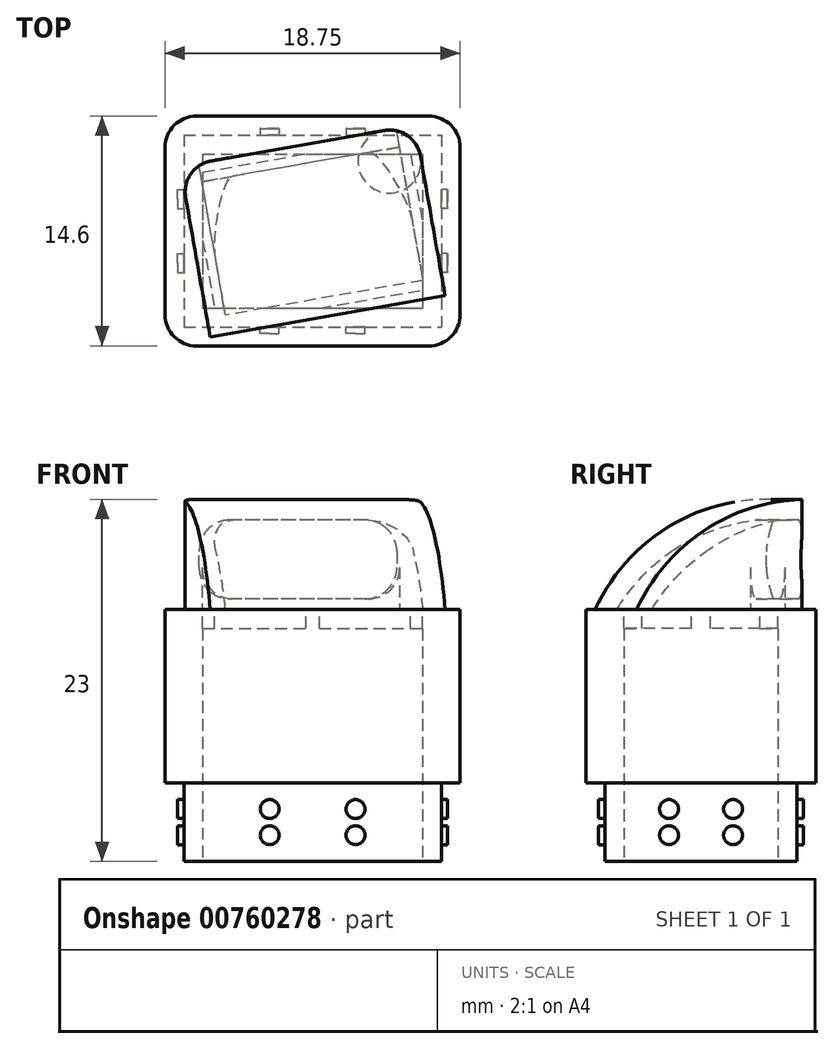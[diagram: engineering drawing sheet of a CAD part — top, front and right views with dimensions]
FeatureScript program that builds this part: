
annotation { "Feature Type Name" : "Feature", "Feature Type Description" : "" }
export const myFeature = defineFeature(function(context is Context, id is Id, definition is map)
    precondition{}
    {
        {
            var Q0;
            Q0=qCreatedBy(makeId("Top.planeOp"),FACE);
            var sketch = newSketch(context, id + "F0", { "sketchPlane" : qUnion([Q0])});
            skLineSegment(sketch, "E0.bottom", {"start": v(-6.9, 7.84) * mm, "end": v(9.85, 7.84) * mm, "construction": true});
            skLineSegment(sketch, "E0.top", {"start": v(-6.9, -4.76) * mm, "end": v(9.85, -4.76) * mm, "construction": true});
            skLineSegment(sketch, "E0.left", {"start": v(-6.9, 7.84) * mm, "end": v(-6.9, -4.76) * mm, "construction": true});
            skLineSegment(sketch, "E0.right", {"start": v(9.85, 7.84) * mm, "end": v(9.85, -4.76) * mm, "construction": true});
            skLineSegment(sketch, "E1.0", {"start": v(-6.7, 7.64) * mm, "end": v(9.65, 7.64) * mm});
            skLineSegment(sketch, "E1.1", {"start": v(-6.7, 7.64) * mm, "end": v(-6.7, -4.56) * mm});
            skLineSegment(sketch, "E1.2", {"start": v(-6.7, -4.56) * mm, "end": v(9.65, -4.56) * mm});
            skLineSegment(sketch, "E1.3", {"start": v(9.65, 7.64) * mm, "end": v(9.65, -4.56) * mm});
            skLineSegment(sketch, "E2.0", {"start": v(-5.5, 6.44) * mm, "end": v(8.45, 6.44) * mm});
            skLineSegment(sketch, "E2.1", {"start": v(-5.5, 6.44) * mm, "end": v(-5.5, -3.36) * mm});
            skLineSegment(sketch, "E2.2", {"start": v(-5.5, -3.36) * mm, "end": v(8.45, -3.36) * mm});
            skLineSegment(sketch, "E2.3", {"start": v(8.45, 6.44) * mm, "end": v(8.45, -3.36) * mm});
            skSolve(sketch);
        }
        {
            var Q0;
            Q0 = qSketchRegion(id + "F0", true);
            extrude(context, id + "F1", {"entities" : qUnion([Q0]), "depth" : 5 * mm, "offsetDistance" : 25 * mm});
        }
        {
            var Q0;
            Q0=makeQuery(id+"F1.opExtrude","CAP_FACE",FACE,{"disambiguationData":[OSD([sQuery(id+"F0.wireOp",EDGE,"E1.0"),sQuery(id+"F0.wireOp",EDGE,"E1.1"),sQuery(id+"F0.wireOp",EDGE,"E1.2"),sQuery(id+"F0.wireOp",EDGE,"E1.3"),sQuery(id+"F0.wireOp",EDGE,"E2.0"),sQuery(id+"F0.wireOp",EDGE,"E2.1"),sQuery(id+"F0.wireOp",EDGE,"E2.2"),sQuery(id+"F0.wireOp",EDGE,"E2.3")])],"isStart":false});
            var sketch = newSketch(context, id + "F2", { "sketchPlane" : qUnion([Q0])});
            skLineSegment(sketch, "E3.0", {"start": v(-5.5, 6.44) * mm, "end": v(-5.5, -3.36) * mm});
            skLineSegment(sketch, "E3.1", {"start": v(-5.5, 6.44) * mm, "end": v(8.45, 6.44) * mm});
            skLineSegment(sketch, "E3.2", {"start": v(8.45, 6.44) * mm, "end": v(8.45, -3.36) * mm});
            skLineSegment(sketch, "E3.3", {"start": v(-5.5, -3.36) * mm, "end": v(8.45, -3.36) * mm});
            skLineSegment(sketch, "E4.0", {"start": v(-6.7, 7.64) * mm, "end": v(9.65, 7.64) * mm, "construction": true});
            skLineSegment(sketch, "E4.1", {"start": v(-6.7, 7.64) * mm, "end": v(-6.7, -4.56) * mm, "construction": true});
            skLineSegment(sketch, "E4.2", {"start": v(-6.7, -4.56) * mm, "end": v(9.65, -4.56) * mm, "construction": true});
            skLineSegment(sketch, "E4.3", {"start": v(9.65, 7.64) * mm, "end": v(9.65, -4.56) * mm, "construction": true});
            skLineSegment(sketch, "E5.0", {"start": v(-7.9, 8.84) * mm, "end": v(10.85, 8.84) * mm});
            skLineSegment(sketch, "E5.1", {"start": v(-7.9, 8.84) * mm, "end": v(-7.9, -5.76) * mm});
            skLineSegment(sketch, "E5.2", {"start": v(-7.9, -5.76) * mm, "end": v(10.85, -5.76) * mm});
            skLineSegment(sketch, "E5.3", {"start": v(10.85, 8.84) * mm, "end": v(10.85, -5.76) * mm});
            skSolve(sketch);
        }
        {
            var Q0;
            Q0 = qSketchRegion(id + "F2", true);
            extrude(context, id + "F3", {"entities" : qUnion([Q0]), "operationType" : NewBodyOperationType.ADD, "depth" : 9.8 * mm, "offsetDistance" : 25 * mm});
        }
        {
            var Q0;
            Q0=makeQuery(id+"F3.opExtrude","CAP_FACE",FACE,{"disambiguationData":[OSD([sQuery(id+"F2.wireOp",EDGE,"E3.0"),sQuery(id+"F2.wireOp",EDGE,"E3.1"),sQuery(id+"F2.wireOp",EDGE,"E3.2"),sQuery(id+"F2.wireOp",EDGE,"E3.3"),sQuery(id+"F2.wireOp",EDGE,"E5.0"),sQuery(id+"F2.wireOp",EDGE,"E5.1"),sQuery(id+"F2.wireOp",EDGE,"E5.2"),sQuery(id+"F2.wireOp",EDGE,"E5.3")])],"isStart":false});
            var sketch = newSketch(context, id + "F4", { "sketchPlane" : qUnion([Q0])});
            skLineSegment(sketch, "E6.0", {"start": v(-7.9, 8.84) * mm, "end": v(-7.9, -5.76) * mm});
            skLineSegment(sketch, "E6.1", {"start": v(-7.9, 8.84) * mm, "end": v(10.85, 8.84) * mm});
            skLineSegment(sketch, "E6.2", {"start": v(10.85, 8.84) * mm, "end": v(10.85, -5.76) * mm});
            skLineSegment(sketch, "E6.3", {"start": v(-7.9, -5.76) * mm, "end": v(10.85, -5.76) * mm});
            skSolve(sketch);
        }
        {
            var Q0;
            Q0 = qSketchRegion(id + "F4", true);
            extrude(context, id + "F5", {"entities" : qUnion([Q0]), "operationType" : NewBodyOperationType.ADD, "depth" : 1.2 * mm, "offsetDistance" : 25 * mm});
        }
        {
            var Q0;
            Q0=makeQuery(id+"F5.opExtrude","CAP_FACE",FACE,{"disambiguationData":[OSD([sQuery(id+"F4.wireOp",EDGE,"E6.0"),sQuery(id+"F4.wireOp",EDGE,"E6.1"),sQuery(id+"F4.wireOp",EDGE,"E6.2"),sQuery(id+"F4.wireOp",EDGE,"E6.3")])],"isStart":false});
            var sketch = newSketch(context, id + "F6", { "sketchPlane" : qUnion([Q0])});
            skLineSegment(sketch, "E7.0", {"start": v(-7.9, 8.84) * mm, "end": v(-7.9, -5.76) * mm, "construction": true});
            skLineSegment(sketch, "E7.1", {"start": v(-7.9, -5.76) * mm, "end": v(10.85, -5.76) * mm, "construction": true});
            skLineSegment(sketch, "E8.0", {"start": v(-5.5, 6.44) * mm, "end": v(8.45, 6.44) * mm, "construction": true});
            skLineSegment(sketch, "E8.1", {"start": v(-5.5, 6.44) * mm, "end": v(-5.5, -3.36) * mm, "construction": true});
            skLineSegment(sketch, "E8.2", {"start": v(8.45, 6.44) * mm, "end": v(8.45, -3.36) * mm, "construction": true});
            skLineSegment(sketch, "E8.3", {"start": v(-5.5, -3.36) * mm, "end": v(8.45, -3.36) * mm, "construction": true});
            skLineSegment(sketch, "E9", {"start": v(-7.9, 8.84) * mm, "end": v(10.85, -5.76) * mm, "construction": true});
            skLineSegment(sketch, "E10.bottom", {"start": v(9.2, -2.08) * mm, "end": v(-4.54, -4.5) * mm, "construction": true});
            skLineSegment(sketch, "E10.top", {"start": v(7.5, 7.57) * mm, "end": v(-6.24, 5.15) * mm, "construction": true});
            skLineSegment(sketch, "E10.left", {"start": v(9.2, -2.08) * mm, "end": v(7.5, 7.57) * mm, "construction": true});
            skLineSegment(sketch, "E10.right", {"start": v(-4.54, -4.5) * mm, "end": v(-6.24, 5.15) * mm, "construction": true});
            skPoint(sketch, "E10.middle", {"position": v(1.48, 1.54) * mm});
            skLineSegment(sketch, "E11.0", {"start": v(-5.03, -5.2) * mm, "end": v(-6.94, 5.64) * mm});
            skLineSegment(sketch, "E11.1", {"start": v(9.9, -2.57) * mm, "end": v(-5.03, -5.2) * mm});
            skLineSegment(sketch, "E11.2", {"start": v(9.9, -2.57) * mm, "end": v(7.98, 8.27) * mm});
            skLineSegment(sketch, "E11.3", {"start": v(7.98, 8.27) * mm, "end": v(-6.94, 5.64) * mm});
            skLineSegment(sketch, "E12.0", {"start": v(-4.05, -3.8) * mm, "end": v(-5.55, 4.66) * mm});
            skLineSegment(sketch, "E12.1", {"start": v(8.5, -1.6) * mm, "end": v(-4.05, -3.8) * mm});
            skLineSegment(sketch, "E12.2", {"start": v(8.5, -1.6) * mm, "end": v(7, 6.88) * mm});
            skLineSegment(sketch, "E12.3", {"start": v(7, 6.88) * mm, "end": v(-5.55, 4.66) * mm});
            skSolve(sketch);
        }
        {
            var Q0;
            Q0 = qSketchRegion(id + "F6", true);
            extrude(context, id + "F7", {"entities" : qUnion([Q0]), "operationType" : NewBodyOperationType.ADD, "depth" : 7 * mm, "offsetDistance" : 25 * mm});
        }
        {
            var Q0;
            {var subQ0=sQuery(id+"F4.wireOp",EDGE,"E6.3");var subQ1=sQuery(id+"F4.wireOp",EDGE,"E6.0");var subQ2=sQuery(id+"F4.wireOp",EDGE,"E6.1");var subQ3=sQuery(id+"F4.wireOp",EDGE,"E6.2");Q0=makeQuery(id+"F7.boolean.opBoolean","SPLIT",FACE,{"disambiguationData":[TD([makeQuery(id+"F3.opExtrude","SWEPT_FACE",FACE,{"disambiguationData":[OSD([sQuery(id+"F2.wireOp",EDGE,"E5.0")])]})])],"derivedFrom":makeQuery(id+"F5.opExtrude","CAP_FACE",FACE,{"disambiguationData":[OSD([subQ1,subQ2,subQ3,subQ0])],"isStart":false})});}
            var sketch = newSketch(context, id + "F8", { "sketchPlane" : qUnion([Q0])});
            skLineSegment(sketch, "E13.0", {"start": v(1.05, 6.44) * mm, "end": v(-5.5, 5.28) * mm});
            skLineSegment(sketch, "E13.1", {"start": v(8.45, -2.2) * mm, "end": v(1.9, -3.36) * mm});
            skLineSegment(sketch, "E13.2", {"start": v(-4.74, -3.36) * mm, "end": v(-5.5, 0.93) * mm});
            skLineSegment(sketch, "E13.3", {"start": v(8.45, 2.15) * mm, "end": v(7.7, 6.44) * mm});
            skLineSegment(sketch, "E14.0", {"start": v(1.05, 6.44) * mm, "end": v(7.7, 6.44) * mm});
            skLineSegment(sketch, "E14.1", {"start": v(-5.5, 6.44) * mm, "end": v(-5.5, 0.93) * mm});
            skLineSegment(sketch, "E14.2", {"start": v(8.45, 2.15) * mm, "end": v(8.45, -2.2) * mm});
            skLineSegment(sketch, "E14.3", {"start": v(-4.74, -3.36) * mm, "end": v(1.9, -3.36) * mm});
            skPoint(sketch, "E15.orphan", {"position": v(-5.5, 6.44) * mm});
            skPoint(sketch, "E16.orphan", {"position": v(-6.24, 5.15) * mm});
            skPoint(sketch, "E17.orphan", {"position": v(-5.5, -3.36) * mm});
            skPoint(sketch, "E18.orphan", {"position": v(-4.54, -4.5) * mm});
            skPoint(sketch, "E19.orphan", {"position": v(8.45, -3.36) * mm});
            skPoint(sketch, "E20.orphan", {"position": v(9.2, -2.08) * mm});
            skPoint(sketch, "E21.orphan", {"position": v(8.45, 6.44) * mm});
            skPoint(sketch, "E22.orphan", {"position": v(7.5, 7.57) * mm});
            skSolve(sketch);
        }
        {
            var Q0;
            Q0 = qSketchRegion(id + "F8", true);
            var Q1;
            Q1=makeQuery(id+"F5.opExtrude","CAP_FACE",FACE,{"disambiguationData":[OSD([sQuery(id+"F4.wireOp",EDGE,"E6.0"),sQuery(id+"F4.wireOp",EDGE,"E6.1"),sQuery(id+"F4.wireOp",EDGE,"E6.2"),sQuery(id+"F4.wireOp",EDGE,"E6.3")])],"isStart":true});
            extrude(context, id + "F9", {"entities" : qUnion([Q0]), "operationType" : NewBodyOperationType.REMOVE, "endBound" : BoundingType.UP_TO_SURFACE, "oppositeDirection" : true, "depth" : 25 * mm, "endBoundEntityFace" : qUnion([Q1]), "offsetDistance" : 25 * mm});
        }
        {
            var Q0;
            Q0=makeQuery(id+"F7.opExtrude","SWEPT_FACE",FACE,{"disambiguationData":[OSD([sQuery(id+"F6.wireOp",EDGE,"E11.0")])]});
            var sketch = newSketch(context, id + "F10", { "sketchPlane" : qUnion([Q0])});
            skLineSegment(sketch, "E23.0", {"start": v(-6.76, 23) * mm, "end": v(-6.76, 16) * mm, "construction": true});
            skLineSegment(sketch, "E23.1", {"start": v(4.24, 23) * mm, "end": v(4.24, 16) * mm, "construction": true});
            skArc(sketch, "E24", {"start": v(4.24, 16) * mm, "mid": v(-0.24, 21.1) * mm, "end": v(-6.76, 23) * mm});
            skArc(sketch, "E25", {"start": v(3.04, 16) * mm, "mid": v(-1.13, 20.12) * mm, "end": v(-6.76, 21.8) * mm});
            skLineSegment(sketch, "E26", {"start": v(4.24, 16) * mm, "end": v(3.04, 16) * mm});
            skLineSegment(sketch, "E27", {"start": v(-6.76, 23) * mm, "end": v(-6.76, 21.8) * mm});
            skSolve(sketch);
        }
        {
            var Q0;
            Q0 = qSketchRegion(id + "F10", true);
            var Q1;
            Q1=makeQuery(id+"F7.opExtrude","SWEPT_FACE",FACE,{"disambiguationData":[OSD([sQuery(id+"F6.wireOp",EDGE,"E11.2")])]});
            extrude(context, id + "F11", {"entities" : qUnion([Q0]), "operationType" : NewBodyOperationType.ADD, "endBound" : BoundingType.UP_TO_SURFACE, "oppositeDirection" : true, "depth" : 25 * mm, "endBoundEntityFace" : qUnion([Q1]), "offsetDistance" : 25 * mm});
        }
        {
            var Q0;
            Q0=makeQuery(id+"F10.imprint","IMPRINT",FACE,{"disambiguationData":[TD([[makeQuery(id+"F10.imprint","IMPRINT",EDGE,{"derivedFrom":sQuery(id+"F10.wireOp",EDGE,"E24")}),-1.0]])]});
            var sketch = newSketch(context, id + "F12", { "sketchPlane" : qUnion([Q0])});
            skLineSegment(sketch, "E28.0", {"start": v(4.24, 23) * mm, "end": v(-6.76, 23) * mm});
            skLineSegment(sketch, "E28.1", {"start": v(4.24, 23) * mm, "end": v(4.24, 16) * mm});
            skArc(sketch, "E28.2", {"start": v(4.24, 16) * mm, "mid": v(-0.24, 21.1) * mm, "end": v(-6.76, 23) * mm});
            skSolve(sketch);
        }
        {
            var Q0;
            Q0 = qSketchRegion(id + "F12", true);
            var Q1;
            Q1=makeQuery(id+"F7.opExtrude","SWEPT_FACE",FACE,{"disambiguationData":[OSD([sQuery(id+"F6.wireOp",EDGE,"E11.2")])]});
            extrude(context, id + "F13", {"entities" : qUnion([Q0]), "operationType" : NewBodyOperationType.REMOVE, "endBound" : BoundingType.UP_TO_SURFACE, "oppositeDirection" : true, "depth" : 25 * mm, "endBoundEntityFace" : qUnion([Q1]), "offsetDistance" : 25 * mm});
        }
        {
            var Q0;
            Q0=makeQuery(id+"F7.opExtrude","SWEPT_FACE",FACE,{"disambiguationData":[OSD([sQuery(id+"F6.wireOp",EDGE,"E11.3")])]});
            var sketch = newSketch(context, id + "F14", { "sketchPlane" : qUnion([Q0])});
            skLineSegment(sketch, "E29.0", {"start": v(-8.1, 21.68) * mm, "end": v(4.65, 21.68) * mm});
            skLineSegment(sketch, "E29.1", {"start": v(4.65, 21.68) * mm, "end": v(4.65, 16.68) * mm});
            skLineSegment(sketch, "E29.2", {"start": v(-8.1, 21.68) * mm, "end": v(-8.1, 16.68) * mm});
            skLineSegment(sketch, "E30", {"start": v(-8.1, 16.68) * mm, "end": v(4.65, 16.68) * mm});
            skPoint(sketch, "E31.orphan", {"position": v(-8.1, 16) * mm});
            skPoint(sketch, "E32.orphan", {"position": v(4.65, 16) * mm});
            skSolve(sketch);
        }
        {
            var Q0;
            Q0 = qSketchRegion(id + "F14", true);
            extrude(context, id + "F15", {"entities" : qUnion([Q0]), "operationType" : NewBodyOperationType.REMOVE, "endBound" : BoundingType.UP_TO_NEXT, "oppositeDirection" : true, "depth" : 25 * mm, "offsetDistance" : 25 * mm});
        }
        {
            var Q0;
            Q0=makeQuery(id+"F5.boolean.opBoolean","MERGE",EDGE,{"derivedFrom":[makeQuery(id+"F3.opExtrude","SWEPT_EDGE",EDGE,{"disambiguationData":[OSD([sQuery(id+"F2.wireOp",EDGE,"E5.0"),sQuery(id+"F2.wireOp",EDGE,"E5.1")])]}),makeQuery(id+"F5.opExtrude","SWEPT_EDGE",EDGE,{"disambiguationData":[OSD([sQuery(id+"F4.wireOp",EDGE,"E6.0"),sQuery(id+"F4.wireOp",EDGE,"E6.1")])]})]});
            var Q1;
            Q1=makeQuery(id+"F5.boolean.opBoolean","MERGE",EDGE,{"derivedFrom":[makeQuery(id+"F3.opExtrude","SWEPT_EDGE",EDGE,{"disambiguationData":[OSD([sQuery(id+"F2.wireOp",EDGE,"E5.1"),sQuery(id+"F2.wireOp",EDGE,"E5.2")])]}),makeQuery(id+"F5.opExtrude","SWEPT_EDGE",EDGE,{"disambiguationData":[OSD([sQuery(id+"F4.wireOp",EDGE,"E6.0"),sQuery(id+"F4.wireOp",EDGE,"E6.3")])]})]});
            var Q2;
            Q2=makeQuery(id+"F5.boolean.opBoolean","MERGE",EDGE,{"derivedFrom":[makeQuery(id+"F3.opExtrude","SWEPT_EDGE",EDGE,{"disambiguationData":[OSD([sQuery(id+"F2.wireOp",EDGE,"E5.0"),sQuery(id+"F2.wireOp",EDGE,"E5.3")])]}),makeQuery(id+"F5.opExtrude","SWEPT_EDGE",EDGE,{"disambiguationData":[OSD([sQuery(id+"F4.wireOp",EDGE,"E6.1"),sQuery(id+"F4.wireOp",EDGE,"E6.2")])]})]});
            var Q3;
            Q3=makeQuery(id+"F5.boolean.opBoolean","MERGE",EDGE,{"derivedFrom":[makeQuery(id+"F3.opExtrude","SWEPT_EDGE",EDGE,{"disambiguationData":[OSD([sQuery(id+"F2.wireOp",EDGE,"E5.2"),sQuery(id+"F2.wireOp",EDGE,"E5.3")])]}),makeQuery(id+"F5.opExtrude","SWEPT_EDGE",EDGE,{"disambiguationData":[OSD([sQuery(id+"F4.wireOp",EDGE,"E6.2"),sQuery(id+"F4.wireOp",EDGE,"E6.3")])]})]});
            var Q4;
            Q4=makeQuery(id+"F7.opExtrude","SWEPT_EDGE",EDGE,{"disambiguationData":[OSD([sQuery(id+"F6.wireOp",EDGE,"E11.2"),sQuery(id+"F6.wireOp",EDGE,"E11.3")])]});
            var Q5;
            Q5=makeQuery(id+"F7.opExtrude","SWEPT_EDGE",EDGE,{"disambiguationData":[OSD([sQuery(id+"F6.wireOp",EDGE,"E11.0"),sQuery(id+"F6.wireOp",EDGE,"E11.3")])]});
            fillet(context, id + "F16", {"entities" : qUnion([Q0, Q1, Q2, Q3, Q4, Q5]), "radius" : 2 * mm, "tangentPropagation" : true, "allowEdgeOverflow" : false});
        }
        {
            var Q0;
            Q0=makeQuery(id+"F15.boolean.opBoolean","COPY",EDGE,{"derivedFrom":makeQuery(id+"F15.opExtrude","SWEPT_EDGE",EDGE,{"disambiguationData":[OSD([sQuery(id+"F14.wireOp",EDGE,"E29.2"),sQuery(id+"F14.wireOp",EDGE,"E30")])]})});
            var Q1;
            Q1=makeQuery(id+"F15.boolean.opBoolean","COPY",EDGE,{"derivedFrom":makeQuery(id+"F15.opExtrude","SWEPT_EDGE",EDGE,{"disambiguationData":[OSD([sQuery(id+"F14.wireOp",EDGE,"E29.0"),sQuery(id+"F14.wireOp",EDGE,"E29.2")])]})});
            var Q2;
            Q2=makeQuery(id+"F15.boolean.opBoolean","COPY",EDGE,{"derivedFrom":makeQuery(id+"F15.opExtrude","SWEPT_EDGE",EDGE,{"disambiguationData":[OSD([sQuery(id+"F14.wireOp",EDGE,"E29.0"),sQuery(id+"F14.wireOp",EDGE,"E29.1")])]})});
            var Q3;
            Q3=makeQuery(id+"F15.boolean.opBoolean","COPY",EDGE,{"derivedFrom":makeQuery(id+"F15.opExtrude","SWEPT_EDGE",EDGE,{"disambiguationData":[OSD([sQuery(id+"F14.wireOp",EDGE,"E29.1"),sQuery(id+"F14.wireOp",EDGE,"E30")])]})});
            fillet(context, id + "F17", {"entities" : qUnion([Q0, Q1, Q2, Q3]), "radius" : 2 * mm, "tangentPropagation" : true, "allowEdgeOverflow" : false});
        }
        {
            var Q0;
            Q0=makeQuery(id+"F1.opExtrude","SWEPT_FACE",FACE,{"disambiguationData":[OSD([sQuery(id+"F0.wireOp",EDGE,"E1.0")])]});
            var sketch = newSketch(context, id + "F18", { "sketchPlane" : qUnion([Q0])});
            skLineSegment(sketch, "E33.0", {"start": v(-9.65, 5) * mm, "end": v(-9.65, 0) * mm, "construction": true});
            skLineSegment(sketch, "E33.1", {"start": v(6.7, 0) * mm, "end": v(-9.65, 0) * mm, "construction": true});
            skLineSegment(sketch, "E34", {"start": v(-9.65, 1.67) * mm, "end": v(6.7, 1.67) * mm, "construction": true});
            skLineSegment(sketch, "E35", {"start": v(6.7, 0) * mm, "end": v(6.7, 1.67) * mm, "construction": true});
            skLineSegment(sketch, "E36", {"start": v(-9.65, 3.33) * mm, "end": v(6.7, 3.33) * mm, "construction": true});
            skLineSegment(sketch, "E37", {"start": v(6.7, 1.67) * mm, "end": v(6.7, 3.33) * mm, "construction": true});
            skLineSegment(sketch, "E38", {"start": v(6.7, 3.33) * mm, "end": v(6.7, 5) * mm, "construction": true});
            skLineSegment(sketch, "E39", {"start": v(-4.2, 5) * mm, "end": v(-4.2, 0) * mm, "construction": true});
            skLineSegment(sketch, "E40", {"start": v(1.25, 5) * mm, "end": v(1.25, 0) * mm, "construction": true});
            skLineSegment(sketch, "E41", {"start": v(-9.65, 5) * mm, "end": v(-4.2, 5) * mm});
            skLineSegment(sketch, "E42", {"start": v(-4.2, 5) * mm, "end": v(1.25, 5) * mm});
            skLineSegment(sketch, "E43", {"start": v(1.25, 5) * mm, "end": v(6.7, 5) * mm});
            skCircle(sketch, "E44", {"center": v(-4.2, 3.33) * mm, "radius": 0.6 * mm});
            skCircle(sketch, "E45", {"center": v(-4.2, 1.67) * mm, "radius": 0.6 * mm});
            skCircle(sketch, "E46", {"center": v(1.25, 3.33) * mm, "radius": 0.6 * mm});
            skCircle(sketch, "E47", {"center": v(1.25, 1.67) * mm, "radius": 0.6 * mm});
            skSolve(sketch);
        }
        {
            var Q0;
            Q0 = qSketchRegion(id + "F18", true);
            extrude(context, id + "F19", {"entities" : qUnion([Q0]), "operationType" : NewBodyOperationType.ADD, "depth" : 0.4 * mm, "offsetDistance" : 25 * mm});
        }
        {
            var Q0;
            Q0=makeQuery(id+"F1.opExtrude","SWEPT_FACE",FACE,{"disambiguationData":[OSD([sQuery(id+"F0.wireOp",EDGE,"E1.2")])]});
            var sketch = newSketch(context, id + "F20", { "sketchPlane" : qUnion([Q0])});
            skLineSegment(sketch, "E48.0", {"start": v(-6.7, 5) * mm, "end": v(-6.7, 0) * mm, "construction": true});
            skLineSegment(sketch, "E48.1", {"start": v(9.65, 0) * mm, "end": v(-6.7, 0) * mm, "construction": true});
            skLineSegment(sketch, "E49", {"start": v(-6.7, 1.67) * mm, "end": v(9.65, 1.67) * mm, "construction": true});
            skLineSegment(sketch, "E50", {"start": v(9.65, 0) * mm, "end": v(9.65, 1.67) * mm, "construction": true});
            skLineSegment(sketch, "E51", {"start": v(-6.7, 3.33) * mm, "end": v(9.65, 3.33) * mm, "construction": true});
            skLineSegment(sketch, "E52", {"start": v(9.65, 1.67) * mm, "end": v(9.65, 3.33) * mm, "construction": true});
            skLineSegment(sketch, "E53", {"start": v(9.65, 3.33) * mm, "end": v(9.65, 5) * mm, "construction": true});
            skLineSegment(sketch, "E54", {"start": v(-1.25, 5) * mm, "end": v(-1.25, 0) * mm, "construction": true});
            skLineSegment(sketch, "E55", {"start": v(4.2, 5) * mm, "end": v(4.2, 0) * mm, "construction": true});
            skLineSegment(sketch, "E56", {"start": v(-6.7, 5) * mm, "end": v(-1.25, 5) * mm, "construction": true});
            skLineSegment(sketch, "E57", {"start": v(-1.25, 5) * mm, "end": v(4.2, 5) * mm, "construction": true});
            skLineSegment(sketch, "E58", {"start": v(4.2, 5) * mm, "end": v(9.65, 5) * mm, "construction": true});
            skCircle(sketch, "E59", {"center": v(-1.25, 3.33) * mm, "radius": 0.6 * mm});
            skCircle(sketch, "E60", {"center": v(-1.25, 1.67) * mm, "radius": 0.6 * mm});
            skCircle(sketch, "E61", {"center": v(4.2, 3.33) * mm, "radius": 0.6 * mm});
            skCircle(sketch, "E62", {"center": v(4.2, 1.67) * mm, "radius": 0.6 * mm});
            skLineSegment(sketch, "E63.0", {"start": v(-6.7, 5) * mm, "end": v(9.65, 5) * mm, "construction": true});
            skSolve(sketch);
        }
        {
            var Q0;
            Q0 = qSketchRegion(id + "F20", true);
            extrude(context, id + "F21", {"entities" : qUnion([Q0]), "operationType" : NewBodyOperationType.ADD, "depth" : 0.4 * mm, "offsetDistance" : 25 * mm});
        }
        {
            var Q0;
            Q0=makeQuery(id+"F1.opExtrude","SWEPT_FACE",FACE,{"disambiguationData":[OSD([sQuery(id+"F0.wireOp",EDGE,"E1.1")])]});
            var sketch = newSketch(context, id + "F22", { "sketchPlane" : qUnion([Q0])});
            skLineSegment(sketch, "E64.0", {"start": v(-7.64, 5) * mm, "end": v(-7.64, 0) * mm, "construction": true});
            skLineSegment(sketch, "E64.1", {"start": v(4.56, 0) * mm, "end": v(-7.64, 0) * mm, "construction": true});
            skLineSegment(sketch, "E65", {"start": v(-7.64, 1.67) * mm, "end": v(4.56, 1.67) * mm, "construction": true});
            skLineSegment(sketch, "E66", {"start": v(4.56, 0) * mm, "end": v(4.56, 1.67) * mm, "construction": true});
            skLineSegment(sketch, "E67", {"start": v(-7.64, 3.33) * mm, "end": v(4.56, 3.33) * mm, "construction": true});
            skLineSegment(sketch, "E68", {"start": v(4.56, 1.67) * mm, "end": v(4.56, 3.33) * mm, "construction": true});
            skLineSegment(sketch, "E69", {"start": v(4.56, 3.33) * mm, "end": v(4.56, 5) * mm, "construction": true});
            skLineSegment(sketch, "E70", {"start": v(-3.57, 5) * mm, "end": v(-3.57, 0) * mm, "construction": true});
            skLineSegment(sketch, "E71", {"start": v(0.5, 5) * mm, "end": v(0.5, 0) * mm, "construction": true});
            skLineSegment(sketch, "E72", {"start": v(-7.64, 5) * mm, "end": v(-3.57, 5) * mm});
            skLineSegment(sketch, "E73", {"start": v(-3.57, 5) * mm, "end": v(0.5, 5) * mm});
            skLineSegment(sketch, "E74", {"start": v(0.5, 5) * mm, "end": v(4.56, 5) * mm});
            skCircle(sketch, "E75", {"center": v(-3.57, 3.33) * mm, "radius": 0.6 * mm});
            skCircle(sketch, "E76", {"center": v(-3.57, 1.67) * mm, "radius": 0.6 * mm});
            skCircle(sketch, "E77", {"center": v(0.5, 3.33) * mm, "radius": 0.6 * mm});
            skCircle(sketch, "E78", {"center": v(0.5, 1.67) * mm, "radius": 0.6 * mm});
            skLineSegment(sketch, "E79.1", {"start": v(-7.64, 5) * mm, "end": v(4.56, 5) * mm, "construction": true});
            skSolve(sketch);
        }
        {
            var Q0;
            Q0 = qSketchRegion(id + "F22", true);
            extrude(context, id + "F23", {"entities" : qUnion([Q0]), "operationType" : NewBodyOperationType.ADD, "depth" : 0.4 * mm, "offsetDistance" : 25 * mm});
        }
        {
            var Q0;
            Q0=makeQuery(id+"F1.opExtrude","SWEPT_FACE",FACE,{"disambiguationData":[OSD([sQuery(id+"F0.wireOp",EDGE,"E1.3")])]});
            var sketch = newSketch(context, id + "F24", { "sketchPlane" : qUnion([Q0])});
            skLineSegment(sketch, "E80.0", {"start": v(-4.56, 5) * mm, "end": v(-4.56, 0) * mm, "construction": true});
            skLineSegment(sketch, "E80.1", {"start": v(7.64, 0) * mm, "end": v(-4.56, 0) * mm, "construction": true});
            skLineSegment(sketch, "E81", {"start": v(-4.56, 1.67) * mm, "end": v(7.64, 1.67) * mm, "construction": true});
            skLineSegment(sketch, "E82", {"start": v(7.64, 0) * mm, "end": v(7.64, 1.67) * mm, "construction": true});
            skLineSegment(sketch, "E83", {"start": v(-4.56, 3.33) * mm, "end": v(7.64, 3.33) * mm, "construction": true});
            skLineSegment(sketch, "E84", {"start": v(7.64, 1.67) * mm, "end": v(7.64, 3.33) * mm, "construction": true});
            skLineSegment(sketch, "E85", {"start": v(7.64, 3.33) * mm, "end": v(7.64, 5) * mm, "construction": true});
            skLineSegment(sketch, "E86", {"start": v(-0.5, 5) * mm, "end": v(-0.5, 0) * mm, "construction": true});
            skLineSegment(sketch, "E87", {"start": v(3.57, 5) * mm, "end": v(3.57, 0) * mm, "construction": true});
            skLineSegment(sketch, "E88", {"start": v(-4.56, 5) * mm, "end": v(-0.5, 5) * mm});
            skLineSegment(sketch, "E89", {"start": v(-0.5, 5) * mm, "end": v(3.57, 5) * mm});
            skLineSegment(sketch, "E90", {"start": v(3.57, 5) * mm, "end": v(7.64, 5) * mm});
            skCircle(sketch, "E91", {"center": v(-0.5, 3.33) * mm, "radius": 0.6 * mm});
            skCircle(sketch, "E92", {"center": v(-0.5, 1.67) * mm, "radius": 0.6 * mm});
            skCircle(sketch, "E93", {"center": v(3.57, 3.33) * mm, "radius": 0.6 * mm});
            skCircle(sketch, "E94", {"center": v(3.57, 1.67) * mm, "radius": 0.6 * mm});
            skLineSegment(sketch, "E95.1", {"start": v(7.64, 5) * mm, "end": v(-4.56, 5) * mm, "construction": true});
            skSolve(sketch);
        }
        {
            var Q0;
            Q0 = qSketchRegion(id + "F24", true);
            extrude(context, id + "F25", {"entities" : qUnion([Q0]), "operationType" : NewBodyOperationType.ADD, "depth" : 0.4 * mm, "offsetDistance" : 25 * mm});
        }
    });
